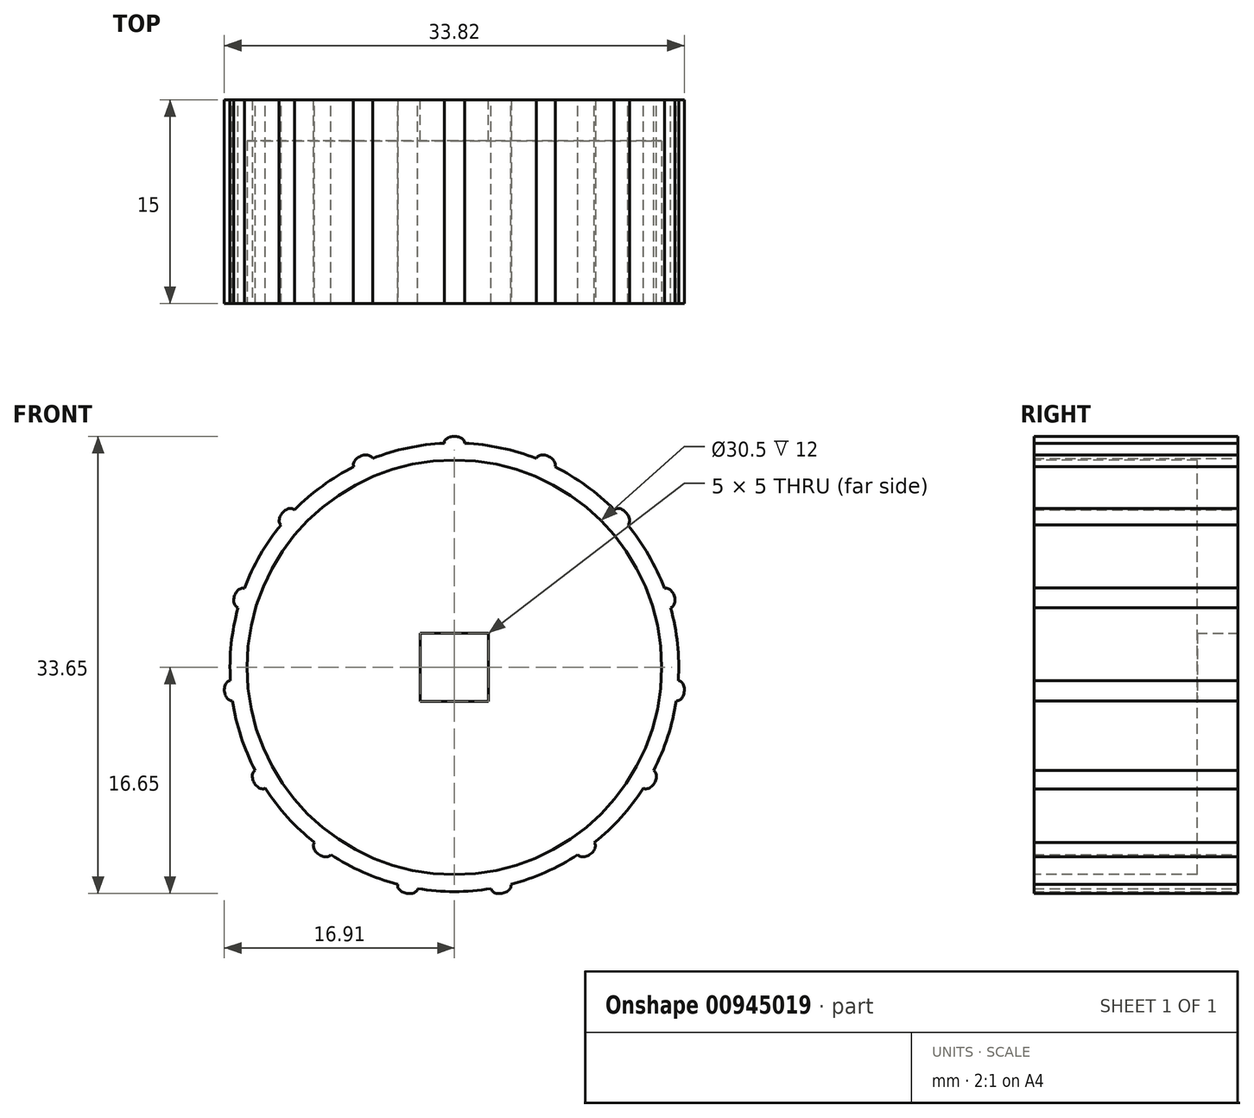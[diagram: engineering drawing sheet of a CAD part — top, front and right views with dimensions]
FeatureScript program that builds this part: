
annotation { "Feature Type Name" : "Feature", "Feature Type Description" : "" }
export const myFeature = defineFeature(function(context is Context, id is Id, definition is map)
    precondition{}
    {
        {
            var Q0;
            Q0=qCreatedBy(makeId("Front.planeOp"),FACE);
            var sketch = newSketch(context, id + "F0", { "sketchPlane" : qUnion([Q0])});
            skCircle(sketch, "E0", {"center": v(0, 0) * mm, "radius": 16.5 * mm});
            skSolve(sketch);
        }
        {
            var Q0;
            Q0=makeQuery(id+"F0.imprint","IMPRINT",FACE,{"disambiguationData":[TD([[makeQuery(id+"F0.imprint","IMPRINT",EDGE,{"derivedFrom":sQuery(id+"F0.wireOp",EDGE,"E0")}),1.0]])]});
            var sketch = newSketch(context, id + "F1", { "sketchPlane" : qUnion([Q0])});
            skSolve(sketch);
        }
        {
            var Q0;
            Q0=makeQuery(id+"F1.imprint","IMPRINT",FACE,{"disambiguationData":[TD([[makeQuery(id+"F1.imprint","IMPRINT",EDGE,{"derivedFrom":makeQuery(id+"F0.imprint","IMPRINT",EDGE,{"derivedFrom":sQuery(id+"F0.wireOp",EDGE,"E0")})}),1.0]])]});
            extrude(context, id + "F2", {"entities" : qUnion([Q0]), "depth" : 15 * mm, "offsetDistance" : 25 * mm});
        }
        {
            var Q0;
            Q0=makeQuery(id+"F2.opExtrude","CAP_FACE",FACE,{"disambiguationData":[OSD([sQuery(id+"F0.wireOp",EDGE,"E0")])],"isStart":false});
            var sketch = newSketch(context, id + "F3", { "sketchPlane" : qUnion([Q0])});
            skCircle(sketch, "E1", {"center": v(0, 0) * mm, "radius": 15.25 * mm});
            skSolve(sketch);
        }
        {
            var Q0;
            Q0 = qSketchRegion(id + "F3", true);
            extrude(context, id + "F4", {"entities" : qUnion([Q0]), "operationType" : NewBodyOperationType.REMOVE, "oppositeDirection" : true, "depth" : 12 * mm, "offsetDistance" : 25 * mm});
        }
        {
            var Q0;
            Q0=makeQuery(id+"F0.imprint","IMPRINT",FACE,{"disambiguationData":[TD([[makeQuery(id+"F0.imprint","IMPRINT",EDGE,{"derivedFrom":sQuery(id+"F0.wireOp",EDGE,"E0")}),1.0]])]});
            var sketch = newSketch(context, id + "F5", { "sketchPlane" : qUnion([Q0])});
            skLineSegment(sketch, "E2", {"start": v(0, 0) * mm, "end": v(0, 16.52) * mm});
            skEllipse(sketch, "E3", {"center": v(0, 16.5) * mm, "majorRadius": 0.75 * mm, "minorRadius": 0.5 * mm, "majorAxis": v(-1, 0)});
            skEllipse(sketch, "E4.1.0", {"center": v(-6.71, 15.07) * mm, "majorRadius": 0.75 * mm, "minorRadius": 0.5 * mm, "majorAxis": v(-0.91, -0.4)});
            skEllipse(sketch, "E4.2.0", {"center": v(-12.26, 11.04) * mm, "majorRadius": 0.75 * mm, "minorRadius": 0.5 * mm, "majorAxis": v(-0.67, -0.74)});
            skEllipse(sketch, "E4.3.0", {"center": v(-15.7, 5.1) * mm, "majorRadius": 0.75 * mm, "minorRadius": 0.5 * mm, "majorAxis": v(-0.3, -0.95)});
            skEllipse(sketch, "E4.4.0", {"center": v(-16.4, -1.72) * mm, "majorRadius": 0.75 * mm, "minorRadius": 0.5 * mm, "majorAxis": v(0.1, -1)});
            skEllipse(sketch, "E4.5.0", {"center": v(-14.29, -8.25) * mm, "majorRadius": 0.75 * mm, "minorRadius": 0.5 * mm, "majorAxis": v(0.5, -0.87)});
            skEllipse(sketch, "E4.6.0", {"center": v(-9.7, -13.35) * mm, "majorRadius": 0.75 * mm, "minorRadius": 0.5 * mm, "majorAxis": v(0.8, -0.59)});
            skEllipse(sketch, "E4.7.0", {"center": v(-3.43, -16.14) * mm, "majorRadius": 0.75 * mm, "minorRadius": 0.5 * mm, "majorAxis": v(0.98, -0.2)});
            skEllipse(sketch, "E4.8.0", {"center": v(3.43, -16.14) * mm, "majorRadius": 0.75 * mm, "minorRadius": 0.5 * mm, "majorAxis": v(0.98, 0.2)});
            skEllipse(sketch, "E4.9.0", {"center": v(9.7, -13.35) * mm, "majorRadius": 0.75 * mm, "minorRadius": 0.5 * mm, "majorAxis": v(0.8, 0.59)});
            skEllipse(sketch, "E4.10.0", {"center": v(14.29, -8.25) * mm, "majorRadius": 0.75 * mm, "minorRadius": 0.5 * mm, "majorAxis": v(0.5, 0.87)});
            skEllipse(sketch, "E4.11.0", {"center": v(16.4, -1.72) * mm, "majorRadius": 0.75 * mm, "minorRadius": 0.5 * mm, "majorAxis": v(0.1, 1)});
            skEllipse(sketch, "E4.12.0", {"center": v(15.7, 5.1) * mm, "majorRadius": 0.75 * mm, "minorRadius": 0.5 * mm, "majorAxis": v(-0.3, 0.95)});
            skEllipse(sketch, "E4.13.0", {"center": v(12.26, 11.04) * mm, "majorRadius": 0.75 * mm, "minorRadius": 0.5 * mm, "majorAxis": v(-0.67, 0.74)});
            skEllipse(sketch, "E4.14.0", {"center": v(6.71, 15.07) * mm, "majorRadius": 0.75 * mm, "minorRadius": 0.5 * mm, "majorAxis": v(-0.91, 0.4)});
            skPoint(sketch, "E4.center", {"position": v(0, 0) * mm});
            skSolve(sketch);
        }
        {
            var Q0;
            Q0 = qSketchRegion(id + "F5", true);
            extrude(context, id + "F6", {"entities" : qUnion([Q0]), "operationType" : NewBodyOperationType.ADD, "depth" : 15 * mm, "offsetDistance" : 25 * mm});
        }
        {
            var Q0;
            Q0=makeQuery(id+"F0.imprint","IMPRINT",FACE,{"disambiguationData":[TD([[makeQuery(id+"F0.imprint","IMPRINT",EDGE,{"derivedFrom":sQuery(id+"F0.wireOp",EDGE,"E0")}),1.0]])]});
            var sketch = newSketch(context, id + "F7", { "sketchPlane" : qUnion([Q0])});
            skLineSegment(sketch, "E5.bottom", {"start": v(2.5, 2.5) * mm, "end": v(-2.5, 2.5) * mm});
            skLineSegment(sketch, "E5.top", {"start": v(2.5, -2.5) * mm, "end": v(-2.5, -2.5) * mm});
            skLineSegment(sketch, "E5.left", {"start": v(2.5, 2.5) * mm, "end": v(2.5, -2.5) * mm});
            skLineSegment(sketch, "E5.right", {"start": v(-2.5, 2.5) * mm, "end": v(-2.5, -2.5) * mm});
            skPoint(sketch, "E5.middle", {"position": v(0, 0) * mm});
            skSolve(sketch);
        }
        {
            var Q0;
            Q0=makeQuery(id+"F7.imprint","IMPRINT",FACE,{"disambiguationData":[TD([[makeQuery(id+"F7.imprint","IMPRINT",EDGE,{"derivedFrom":sQuery(id+"F7.wireOp",EDGE,"E5.bottom")}),1.0]])]});
            extrude(context, id + "F8", {"entities" : qUnion([Q0]), "operationType" : NewBodyOperationType.REMOVE, "depth" : 3 * mm, "offsetDistance" : 25 * mm});
        }
    });
